# Revit family: agtatec_Record_ScrtTnnl_FlipFlowTwin_Standalone2
name_source: partatom
category: Doors
revit_build: Autodesk Revit 2015 (Build: 20140606_1530(x64)
units: mm (PartAtom-declared; Revit-internal decimal feet)

## types (8) — shared parameters
Alarm = agtatec_Record_Glass
AntiFingerTrapRequirement = No
BIMObjectName = agtatec_Record_ScrtTnnl_FlipFlowTwin_Standalone
CanopyHeight = 211.00 mm
Capacity = up tp 2000 people / hour
Color = RAL
Construction Type = Automatic Sliding Door
DoorSeal = Yes
DurationUnit = Year
ElectronicLock = Yes
Finish = Aluminium and Glass
FrameFinishOptions = stainless steel finish
FrameMaterial = agtatec_Record_Aluminium
Frames = agtatec_Record_Aluminium
GlassLayers = 1
GlassThickness1 = 0.00 mm
GlassThickness2 = 0.00 mm
HasDrive = Yes
Height = 2365.00 mm
IfcExportAs = IFCDoorStyle
IfcExportType = Door
Length = 5999.84 mm
ManufacturerURL = www.agta-record.com
Material = Aluminium
ModelReference = depends on the configuration
NBSDescription = Sliding Doorset
NominalHeight = 2365.00 mm
OpenDoor = No
OpeningRotationAngle = 0.00°
Operation = Automatic
PanelGlass = agtatec_Record_Glass
PassageHeight = 2365.00 mm
ProductInformation = www.agta-record.com
ReplacementCost = Depends on the configuration and door type
Rough Height = 0.00 mm
Rubber = agtatec_Record_Rubber
SafetyDevices = YES
SelfClosing = Yes
Sensor = agtatec_Record_Aluminium
Shape = cuboid shaped
SmokeStop = No
Thickness = 0.00 mm
ThresholdRequired = No
ThresholdStripping = No
Uniclass2015Code = Pr_30_59_24_37
Uniclass2015Title = High security doorsets
Uniclass2015Version = 1.9
Version = 1
WarrantyDescription = Depends on country
WarrantyDurationParts = Depends on country
WarrantyDurationUnit = Depends on country
WarrantyGuarantorParts = Local door manufacturer
zero-valued in all types: Cost, Infiltration, ThermalTransmittance

## per-type parameters (varying)
| type | DoorIncluded | Extended | Function | HandicapAccessible | IsExternal | NBSReference | Name | NominalLength | NominalWidth | PanelWidth | PassageWidth | PassageWidthOptions | Rough Width | Size | URL | Width |
| FlipFlow Twin extended_1429 |  | Yes | Exterior | Yes | No | 25-50-20/177 | record FlipFlow Twin extended | 5242.00 mm | 1429.00 mm | 573.10 mm | 1100.00 mm | 650/900/1100/1204 | 1429.00 mm | 2365x5242x1429 |  | 1429.00 mm |
| FlipFlow Twin extended_979 |  | Yes | Exterior | No | Yes | 25-50-20/177 | record FlipFlow Twin extended | 5242.00 mm | 979.00 mm | 348.10 mm | 650.00 mm | 650/900/1100/1204 | 979.00 mm | 2365x5242x979 |  | 979.00 mm |
| FlipFlow Twin_979 | Yes | No | Exterior | No | No | 25-50-20/176 | record FlipFlow Twin | 3526.00 mm | 979.00 mm | 348.10 mm | 650.00 mm | 650/900/1100/1203 | 979.00 mm | 2365x3526x979 |  | 979.00 mm |
| FlipFlow Twin extended_1529 |  | Yes | Exterior | Yes | No | 25-50-20/177 | record FlipFlow Twin extended | 5242.00 mm | 1529.00 mm | 623.10 mm | 1200.00 mm | 650/900/1100/1204 | 1529.00 mm | 2365x5242x1529 |  | 1529.00 mm |
| FlipFlow Twin_1529 |  | No | Exterior | Yes | No | 25-50-20/176 | record FlipFlow Twin | 3526.00 mm | 1529.00 mm | 623.10 mm | 1200.00 mm | 650/900/1100/1203 | 1529.00 mm | 2365x3526x1529 |  | 1529.00 mm |
| FlipFlow Twin_1429 |  | No | Exterior | Yes | No | 25-50-20/176 | record FlipFlow Twin | 3526.00 mm | 1429.00 mm | 573.10 mm | 1100.00 mm | 650/900/1100/1203 | 1429.00 mm | 2365x3526x1429 |  | 1429.00 mm |
| FlipFlow Twin_1229 |  | No | Exterior | Yes | No | 25-50-20/176 | record FlipFlow Twin | 3526.00 mm | 1229.00 mm | 473.10 mm | 900.00 mm | 650/900/1100/1203 | 1229.00 mm | 2365x3526x1229 |  | 1229.00 mm |
| FlipFlow Twin extended_1229 |  | Yes | Interior | Yes | No | 25-50-20/177 | record FlipFlow Twin extended | 5242.00 mm | 1229.00 mm | 473.10 mm | 900.00 mm | 650/900/1100/1204 | 1229.00 mm | 2365x5242x1229 | www.agta-record.com | 1229.00 mm |

## geometry (parser evidence)
native form markers: Blend x2, Sweep x9
no freeform markers — native parametric forms only
